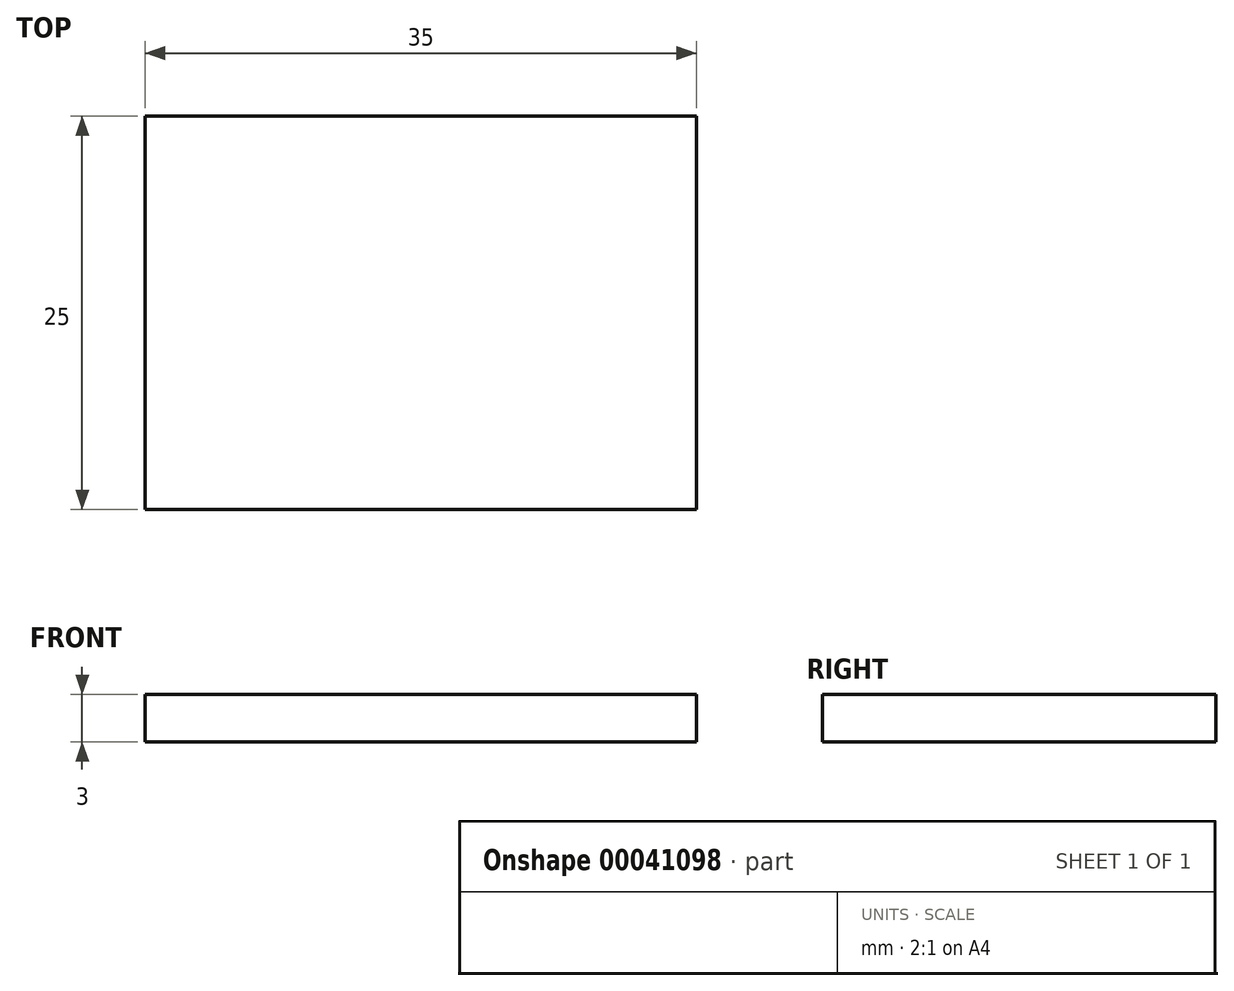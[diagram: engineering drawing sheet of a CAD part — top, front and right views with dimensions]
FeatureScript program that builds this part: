
annotation { "Feature Type Name" : "Feature", "Feature Type Description" : "" }
export const myFeature = defineFeature(function(context is Context, id is Id, definition is map)
    precondition{}
    {
        {
            var Q0;
            Q0=qCreatedBy(makeId("Top.planeOp"),FACE);
            var sketch = newSketch(context, id + "F0", { "sketchPlane" : qUnion([Q0])});
            skLineSegment(sketch, "E0.bottom", {"start": v(0, 0) * mm, "end": v(35, 0) * mm});
            skLineSegment(sketch, "E0.top", {"start": v(0, 25) * mm, "end": v(35, 25) * mm});
            skLineSegment(sketch, "E0.left", {"start": v(0, 0) * mm, "end": v(0, 25) * mm});
            skLineSegment(sketch, "E0.right", {"start": v(35, 0) * mm, "end": v(35, 25) * mm});
            skSolve(sketch);
        }
        {
            var Q0;
            Q0 = qSketchRegion(id + "F0", true);
            extrude(context, id + "F1", {"entities" : qUnion([Q0]), "depth" : 3 * mm});
        }
    });
